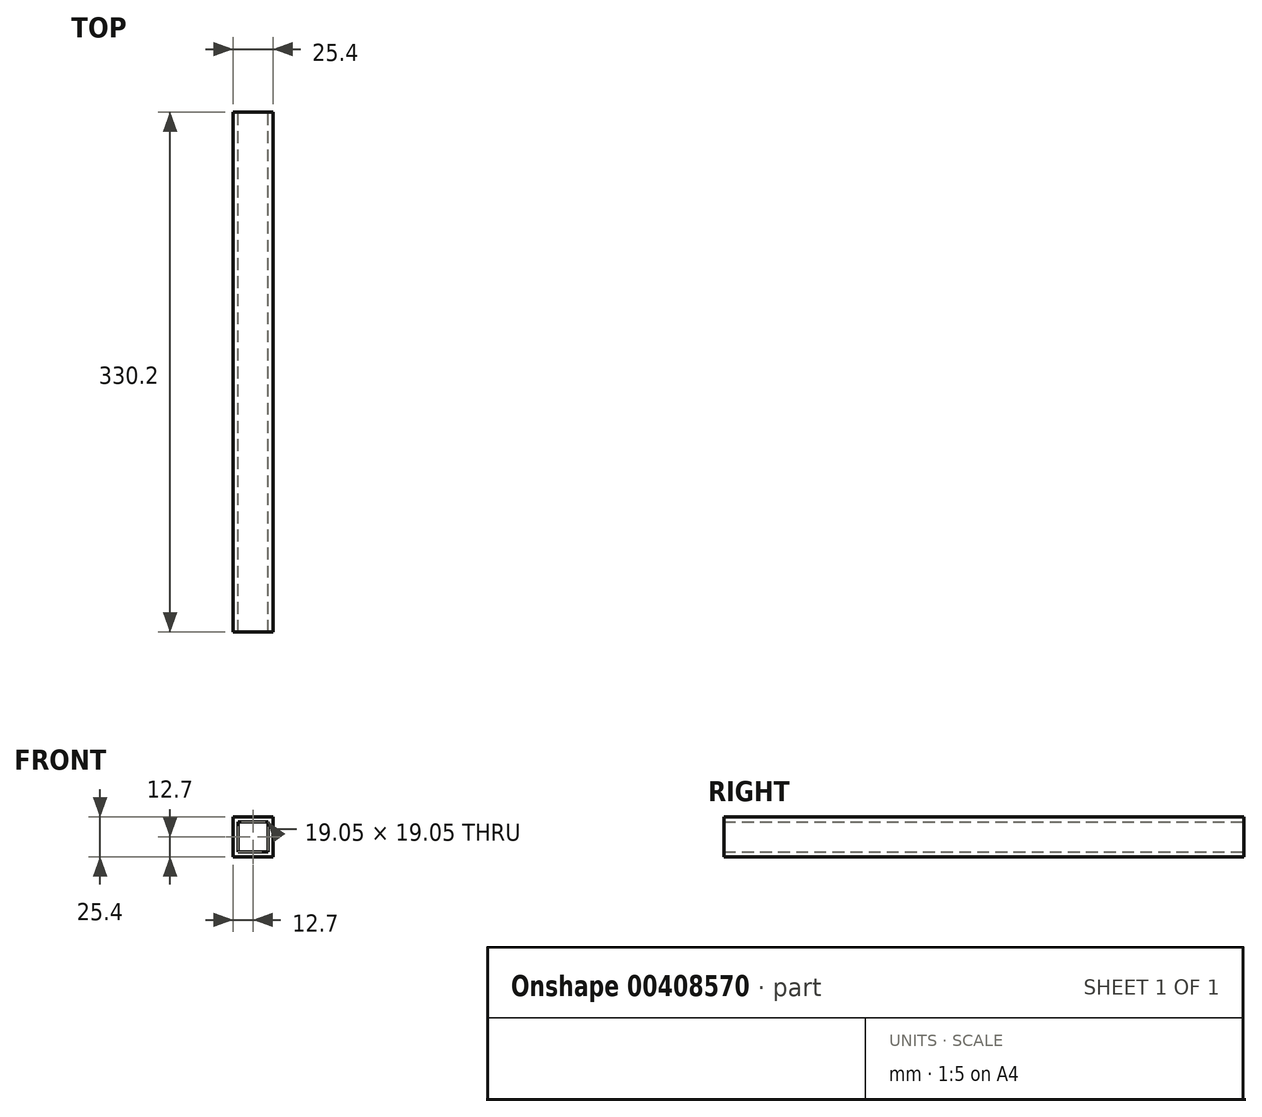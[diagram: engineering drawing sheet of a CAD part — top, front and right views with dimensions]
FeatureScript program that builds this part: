
annotation { "Feature Type Name" : "Feature", "Feature Type Description" : "" }
export const myFeature = defineFeature(function(context is Context, id is Id, definition is map)
    precondition{}
    {
        {
            var Q0;
            Q0=qCreatedBy(makeId("Front.planeOp"),FACE);
            var sketch = newSketch(context, id + "F0", { "sketchPlane" : qUnion([Q0])});
            skLineSegment(sketch, "E0.bottom", {"start": v(0, 0) * mm, "end": v(25.4, 0) * mm});
            skLineSegment(sketch, "E0.top", {"start": v(0, 25.4) * mm, "end": v(25.4, 25.4) * mm});
            skLineSegment(sketch, "E0.left", {"start": v(0, 0) * mm, "end": v(0, 25.4) * mm});
            skLineSegment(sketch, "E0.right", {"start": v(25.4, 0) * mm, "end": v(25.4, 25.4) * mm});
            skLineSegment(sketch, "E1.0", {"start": v(3.17, 22.22) * mm, "end": v(22.22, 22.22) * mm});
            skLineSegment(sketch, "E1.1", {"start": v(3.17, 3.18) * mm, "end": v(3.17, 22.23) * mm});
            skLineSegment(sketch, "E1.2", {"start": v(3.17, 3.18) * mm, "end": v(22.23, 3.18) * mm});
            skLineSegment(sketch, "E1.3", {"start": v(22.23, 3.18) * mm, "end": v(22.22, 22.22) * mm});
            skSolve(sketch);
        }
        {
            var Q0;
            Q0=makeQuery(id+"F0.imprint","IMPRINT",FACE,{"disambiguationData":[TD([[makeQuery(id+"F0.imprint","IMPRINT",EDGE,{"derivedFrom":sQuery(id+"F0.wireOp",EDGE,"E0.bottom")}),1.0]])]});
            extrude(context, id + "F1", {"entities" : qUnion([Q0]), "depth" : 330.2 * mm});
        }
    });
